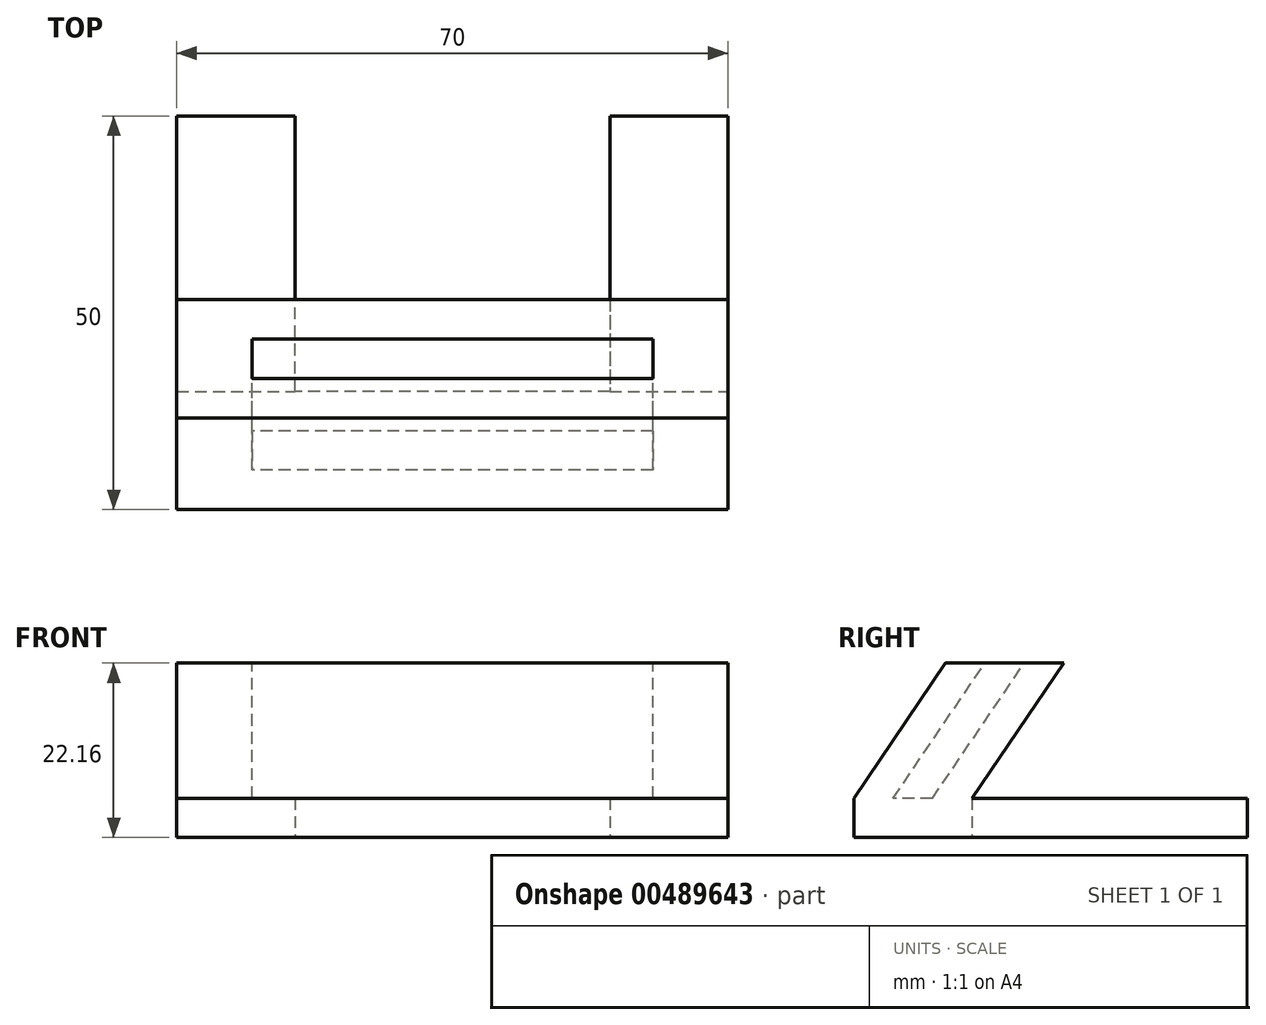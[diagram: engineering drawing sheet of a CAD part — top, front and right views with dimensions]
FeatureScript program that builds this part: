
annotation { "Feature Type Name" : "Feature", "Feature Type Description" : "" }
export const myFeature = defineFeature(function(context is Context, id is Id, definition is map)
    precondition{}
    {
        {
            var Q0;
            Q0=qCreatedBy(makeId("Top.planeOp"),FACE);
            var sketch = newSketch(context, id + "F0", { "sketchPlane" : qUnion([Q0])});
            skLineSegment(sketch, "E0", {"start": v(-3.78, -13.92) * mm, "end": v(66.22, -13.92) * mm});
            skLineSegment(sketch, "E1", {"start": v(66.22, -13.92) * mm, "end": v(66.22, 36.08) * mm});
            skLineSegment(sketch, "E2", {"start": v(66.22, 36.08) * mm, "end": v(51.22, 36.08) * mm});
            skLineSegment(sketch, "E3", {"start": v(51.22, 36.08) * mm, "end": v(51.22, 1.08) * mm});
            skLineSegment(sketch, "E4", {"start": v(51.22, 1.08) * mm, "end": v(11.22, 1.08) * mm});
            skLineSegment(sketch, "E5", {"start": v(11.22, 1.08) * mm, "end": v(11.22, 36.08) * mm});
            skLineSegment(sketch, "E6", {"start": v(11.22, 36.08) * mm, "end": v(-3.78, 36.08) * mm});
            skLineSegment(sketch, "E7", {"start": v(-3.78, 36.08) * mm, "end": v(-3.78, -13.92) * mm});
            skLineSegment(sketch, "E8", {"start": v(11.22, 1.08) * mm, "end": v(11.22, -13.92) * mm, "construction": true});
            skSolve(sketch);
        }
        {
            var Q0;
            Q0 = qSketchRegion(id + "F0", true);
            extrude(context, id + "F1", {"entities" : qUnion([Q0]), "depth" : 5 * mm});
        }
        {
            var Q0;
            Q0=makeQuery(id+"F1.opExtrude","SWEPT_FACE",FACE,{"disambiguationData":[OSD([sQuery(id+"F0.wireOp",EDGE,"E7")])]});
            var sketch = newSketch(context, id + "F2", { "sketchPlane" : qUnion([Q0])});
            skLineSegment(sketch, "E9", {"start": v(13.92, 5) * mm, "end": v(2.26, 22.16) * mm});
            skSolve(sketch);
        }
        {
            var Q0;
            Q0=makeQuery(id+"F1.opExtrude","CAP_FACE",FACE,{"disambiguationData":[OSD([sQuery(id+"F0.wireOp",EDGE,"E0"),sQuery(id+"F0.wireOp",EDGE,"E1"),sQuery(id+"F0.wireOp",EDGE,"E2"),sQuery(id+"F0.wireOp",EDGE,"E3"),sQuery(id+"F0.wireOp",EDGE,"E4"),sQuery(id+"F0.wireOp",EDGE,"E5"),sQuery(id+"F0.wireOp",EDGE,"E6"),sQuery(id+"F0.wireOp",EDGE,"E7")])],"isStart":false});
            var sketch = newSketch(context, id + "F3", { "sketchPlane" : qUnion([Q0])});
            skLineSegment(sketch, "E10.bottom", {"start": v(-3.78, -13.92) * mm, "end": v(66.22, -13.92) * mm});
            skLineSegment(sketch, "E10.top", {"start": v(-3.78, 1.08) * mm, "end": v(66.22, 1.08) * mm});
            skLineSegment(sketch, "E10.left", {"start": v(-3.78, -13.92) * mm, "end": v(-3.78, 1.08) * mm});
            skLineSegment(sketch, "E10.right", {"start": v(66.22, -13.92) * mm, "end": v(66.22, 1.08) * mm});
            skLineSegment(sketch, "E11.bottom", {"start": v(56.68, -3.92) * mm, "end": v(5.77, -3.92) * mm});
            skLineSegment(sketch, "E11.top", {"start": v(56.68, -8.92) * mm, "end": v(5.77, -8.92) * mm});
            skLineSegment(sketch, "E11.left", {"start": v(56.68, -3.92) * mm, "end": v(56.68, -8.92) * mm});
            skLineSegment(sketch, "E11.right", {"start": v(5.77, -3.92) * mm, "end": v(5.77, -8.92) * mm});
            skPoint(sketch, "E11.middle", {"position": v(31.22, -6.42) * mm});
            skPoint(sketch, "E11.middle.positionSnap0", {"position": v(31.22, 1.08) * mm});
            skPoint(sketch, "E11.middle.positionSnap1", {"position": v(-3.78, -6.42) * mm});
            skPoint(sketch, "E11.centerSnap0", {"position": v(31.22, 1.08) * mm});
            skPoint(sketch, "E11.centerSnap1", {"position": v(-3.78, -6.42) * mm});
            skSolve(sketch);
        }
        {
            var Q0;
            Q0 = qSketchRegion(id + "F3", true);
            var Q1;
            Q1 = qConstructionFilter(qBodyType(qCreatedBy(id + "F2" ,EDGE), BodyType.WIRE), ConstructionObject.NO);
            sweep(context, id + "F4", {"operationType" : NewBodyOperationType.ADD, "profiles" : qUnion([Q0]), "path" : qUnion([Q1])});
        }
    });
